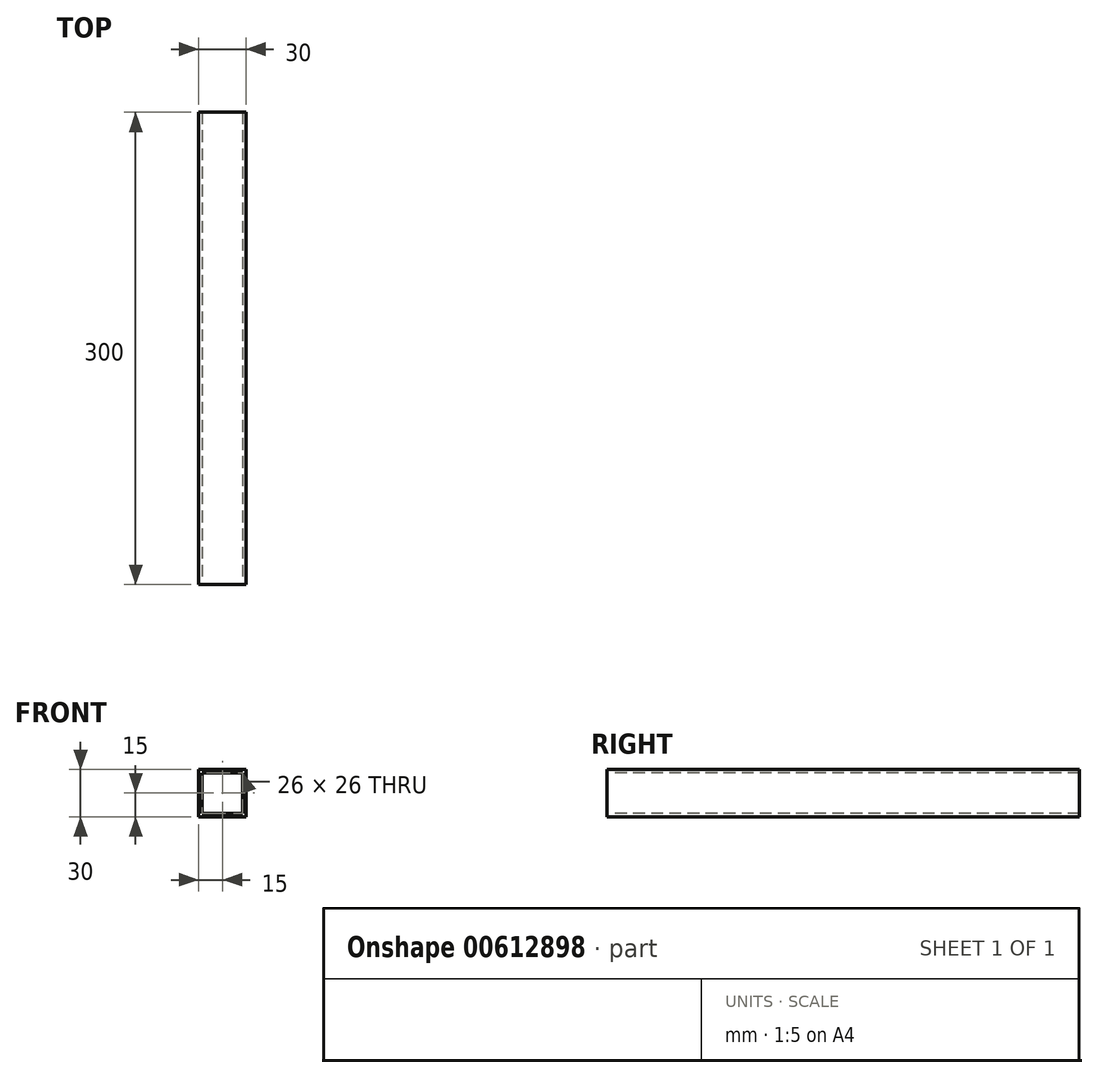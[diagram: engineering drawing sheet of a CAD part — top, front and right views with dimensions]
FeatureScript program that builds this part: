
annotation { "Feature Type Name" : "Feature", "Feature Type Description" : "" }
export const myFeature = defineFeature(function(context is Context, id is Id, definition is map)
    precondition{}
    {
        {
            var Q0;
            Q0=qCreatedBy(makeId("Front.planeOp"),FACE);
            var sketch = newSketch(context, id + "F0", { "sketchPlane" : qUnion([Q0])});
            skLineSegment(sketch, "E0.bottom", {"start": v(0, 0) * mm, "end": v(30, 0) * mm});
            skLineSegment(sketch, "E0.top", {"start": v(0, 30) * mm, "end": v(30, 30) * mm});
            skLineSegment(sketch, "E0.left", {"start": v(0, 0) * mm, "end": v(0, 30) * mm});
            skLineSegment(sketch, "E0.right", {"start": v(30, 0) * mm, "end": v(30, 30) * mm});
            skSolve(sketch);
        }
        {
            var Q0;
            Q0=makeQuery(id+"F0.imprint","IMPRINT",FACE,{"disambiguationData":[TD([[makeQuery(id+"F0.imprint","IMPRINT",EDGE,{"derivedFrom":sQuery(id+"F0.wireOp",EDGE,"E0.bottom")}),1.0]])]});
            var sketch = newSketch(context, id + "F1", { "sketchPlane" : qUnion([Q0])});
            skSolve(sketch);
        }
        {
            var Q0;
            Q0 = qSketchRegion(id + "F1", true);
            var Q1;
            Q1=makeQuery(id+"F0.imprint","IMPRINT",FACE,{"disambiguationData":[TD([[makeQuery(id+"F0.imprint","IMPRINT",EDGE,{"derivedFrom":sQuery(id+"F0.wireOp",EDGE,"E0.bottom")}),1.0]])]});
            extrude(context, id + "F2", {"entities" : qUnion([Q0, Q1]), "depth" : 300 * mm, "offsetDistance" : 25 * mm});
        }
        {
            var Q0;
            Q0=makeQuery(id+"F2.opExtrude","CAP_FACE",FACE,{"disambiguationData":[OSD([sQuery(id+"F0.wireOp",EDGE,"E0.bottom"),sQuery(id+"F0.wireOp",EDGE,"E0.top"),sQuery(id+"F0.wireOp",EDGE,"E0.left"),sQuery(id+"F0.wireOp",EDGE,"E0.right")])],"isStart":false});
            var sketch = newSketch(context, id + "F3", { "sketchPlane" : qUnion([Q0])});
            skLineSegment(sketch, "E1.0", {"start": v(28, 28) * mm, "end": v(2, 28) * mm});
            skLineSegment(sketch, "E1.1", {"start": v(28, 2) * mm, "end": v(28, 28) * mm});
            skLineSegment(sketch, "E1.2", {"start": v(2, 2) * mm, "end": v(28, 2) * mm});
            skLineSegment(sketch, "E1.3", {"start": v(2, 28) * mm, "end": v(2, 2) * mm});
            skSolve(sketch);
        }
        {
            var Q0;
            Q0 = qSketchRegion(id + "F3", true);
            extrude(context, id + "F4", {"entities" : qUnion([Q0]), "operationType" : NewBodyOperationType.REMOVE, "oppositeDirection" : true, "depth" : 300 * mm, "offsetDistance" : 25 * mm});
        }
    });
